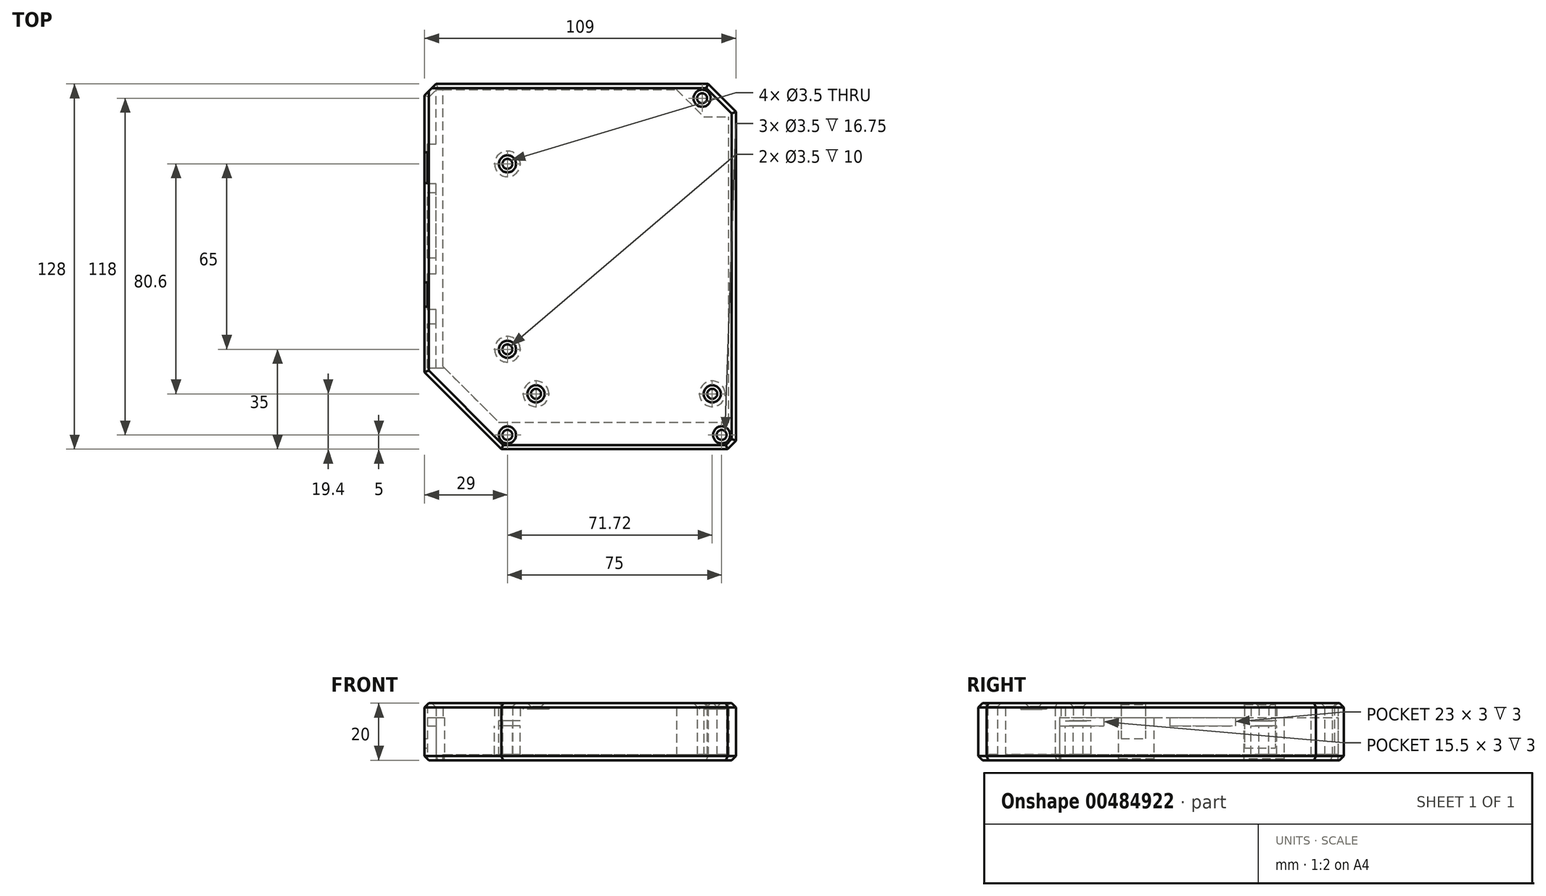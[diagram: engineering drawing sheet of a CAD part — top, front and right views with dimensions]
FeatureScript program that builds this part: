
annotation { "Feature Type Name" : "Feature", "Feature Type Description" : "" }
export const myFeature = defineFeature(function(context is Context, id is Id, definition is map)
    precondition{}
    {
        {
            var Q0;
            Q0=qCreatedBy(makeId("Top.planeOp"),FACE);
            var sketch = newSketch(context, id + "F0", { "sketchPlane" : qUnion([Q0])});
            skLineSegment(sketch, "E0.bottom", {"start": v(-53.5, 61) * mm, "end": v(30.5, 61) * mm, "construction": true});
            skLineSegment(sketch, "E0.top", {"start": v(-53.5, -35) * mm, "end": v(30.5, -35) * mm, "construction": true});
            skLineSegment(sketch, "E0.left", {"start": v(-53.5, 61) * mm, "end": v(-53.5, -35) * mm, "construction": true});
            skLineSegment(sketch, "E0.right", {"start": v(30.5, 61) * mm, "end": v(30.5, -35) * mm, "construction": true});
            skLineSegment(sketch, "E1.bottom", {"start": v(-19.5, 52) * mm, "end": v(51.5, 52) * mm, "construction": true});
            skLineSegment(sketch, "E1.top", {"start": v(-19.5, -54) * mm, "end": v(51.5, -54) * mm, "construction": true});
            skLineSegment(sketch, "E1.left", {"start": v(-19.5, 52) * mm, "end": v(-19.5, -54) * mm, "construction": true});
            skLineSegment(sketch, "E1.right", {"start": v(51.5, 52) * mm, "end": v(51.5, -54) * mm, "construction": true});
            skLineSegment(sketch, "E2.bottom", {"start": v(54.5, 64) * mm, "end": v(-54.5, 64) * mm, "construction": true});
            skLineSegment(sketch, "E2.top", {"start": v(54.5, -64) * mm, "end": v(-54.5, -64) * mm, "construction": true});
            skLineSegment(sketch, "E2.left", {"start": v(54.5, 64) * mm, "end": v(54.5, -64) * mm, "construction": true});
            skLineSegment(sketch, "E2.right", {"start": v(-54.5, 64) * mm, "end": v(-54.5, -64) * mm, "construction": true});
            skPoint(sketch, "E2.middle", {"position": v(0, 0) * mm});
            skPoint(sketch, "E3", {"position": v(-25.5, -29) * mm});
            skPoint(sketch, "E4", {"position": v(-25.5, 36) * mm});
            skPoint(sketch, "E5", {"position": v(-25.5, -59) * mm});
            skPoint(sketch, "E6", {"position": v(49.5, -59) * mm});
            skSolve(sketch);
        }
        {
            var Q0;
            Q0=qCreatedBy(makeId("Top.planeOp"),FACE);
            var sketch = newSketch(context, id + "F1", { "sketchPlane" : qUnion([Q0])});
            skLineSegment(sketch, "E7", {"start": v(-54.5, -37.07) * mm, "end": v(-27.57, -64) * mm});
            skLineSegment(sketch, "E8", {"start": v(-27.57, -64) * mm, "end": v(51.57, -64) * mm});
            skLineSegment(sketch, "E9", {"start": v(51.57, -64) * mm, "end": v(54.5, -61.07) * mm});
            skLineSegment(sketch, "E10", {"start": v(54.5, -61.07) * mm, "end": v(54.5, 54.24) * mm});
            skLineSegment(sketch, "E11", {"start": v(54.5, 54.24) * mm, "end": v(44.74, 64) * mm});
            skLineSegment(sketch, "E12", {"start": v(44.74, 64) * mm, "end": v(-50.5, 64) * mm});
            skLineSegment(sketch, "E13", {"start": v(-54.5, 60) * mm, "end": v(-54.5, -37.07) * mm});
            skCircle(sketch, "E14", {"center": v(42.67, 59) * mm, "radius": 1.75 * mm});
            skCircle(sketch, "E15", {"center": v(-25.5, 36) * mm, "radius": 1.75 * mm});
            skCircle(sketch, "E16", {"center": v(-25.5, -29) * mm, "radius": 1.75 * mm});
            skCircle(sketch, "E17", {"center": v(-25.5, -59) * mm, "radius": 1.75 * mm});
            skCircle(sketch, "E18", {"center": v(49.5, -59) * mm, "radius": 1.75 * mm});
            skLineSegment(sketch, "E19", {"start": v(-48.09, -35) * mm, "end": v(-53.5, -35) * mm, "construction": true});
            skLineSegment(sketch, "E20", {"start": v(-53.5, -35) * mm, "end": v(-53.5, -20) * mm});
            skLineSegment(sketch, "E21", {"start": v(-53.5, -20) * mm, "end": v(-50.5, -20) * mm});
            skLineSegment(sketch, "E22", {"start": v(-50.5, -20) * mm, "end": v(-50.5, -15) * mm});
            skLineSegment(sketch, "E23", {"start": v(-50.5, -15) * mm, "end": v(-53.5, -15) * mm});
            skLineSegment(sketch, "E24", {"start": v(-48.09, -35) * mm, "end": v(-28.59, -54.5) * mm});
            skLineSegment(sketch, "E25", {"start": v(-28.59, -54.5) * mm, "end": v(52, -54.5) * mm});
            skLineSegment(sketch, "E26", {"start": v(52, -54.5) * mm, "end": v(52, 52.5) * mm});
            skLineSegment(sketch, "E27", {"start": v(-53.5, -15) * mm, "end": v(-53.5, -2.5) * mm});
            skLineSegment(sketch, "E28", {"start": v(-53.5, -2.5) * mm, "end": v(-50.5, -2.5) * mm});
            skLineSegment(sketch, "E29", {"start": v(-50.5, -2.5) * mm, "end": v(-50.5, 3) * mm});
            skLineSegment(sketch, "E30", {"start": v(-50.5, 3) * mm, "end": v(-53.5, 3) * mm});
            skLineSegment(sketch, "E31", {"start": v(-53.5, 3) * mm, "end": v(-53.5, 26) * mm});
            skLineSegment(sketch, "E32", {"start": v(-53.5, 26) * mm, "end": v(-50.5, 26) * mm});
            skLineSegment(sketch, "E33", {"start": v(-50.5, 26) * mm, "end": v(-50.5, 29) * mm});
            skLineSegment(sketch, "E34", {"start": v(-50.5, 29) * mm, "end": v(-53.5, 29) * mm});
            skLineSegment(sketch, "E35", {"start": v(-53.5, 29) * mm, "end": v(-53.5, 43) * mm});
            skLineSegment(sketch, "E36", {"start": v(-53.5, 43) * mm, "end": v(-50.5, 43) * mm});
            skLineSegment(sketch, "E37", {"start": v(-50.5, 62) * mm, "end": v(33.74, 62) * mm});
            skLineSegment(sketch, "E38", {"start": v(33.74, 62) * mm, "end": v(43.24, 52.5) * mm});
            skLineSegment(sketch, "E39", {"start": v(43.24, 52.5) * mm, "end": v(52, 52.5) * mm});
            skLineSegment(sketch, "E40", {"start": v(-50.5, 43) * mm, "end": v(-50.5, 50) * mm});
            skLineSegment(sketch, "E41", {"start": v(-53.5, -35) * mm, "end": v(-53.5, -35.5) * mm});
            skLineSegment(sketch, "E42", {"start": v(-53.5, -35.5) * mm, "end": v(-47.59, -35.5) * mm});
            skLineSegment(sketch, "E43", {"start": v(-48.09, -35) * mm, "end": v(-48.09, 62) * mm});
            skCircle(sketch, "E44", {"center": v(-15.5, -44.6) * mm, "radius": 1.75 * mm});
            skCircle(sketch, "E45", {"center": v(46.22, -44.6) * mm, "radius": 1.75 * mm});
            skCircle(sketch, "E46", {"center": v(-25.5, 36) * mm, "radius": 4.5 * mm});
            skCircle(sketch, "E47", {"center": v(-25.5, -29) * mm, "radius": 4.5 * mm});
            skCircle(sketch, "E48", {"center": v(46.22, -44.6) * mm, "radius": 4.5 * mm});
            skCircle(sketch, "E49", {"center": v(-15.5, -44.6) * mm, "radius": 4.5 * mm});
            skLineSegment(sketch, "E50", {"start": v(-50.5, 64) * mm, "end": v(-54.5, 60) * mm});
            skLineSegment(sketch, "E51", {"start": v(-50.5, 50) * mm, "end": v(-50.5, 62) * mm});
            skSolve(sketch);
        }
        {
            var Q0;
            Q0=makeQuery(id+"F1.imprint","IMPRINT",FACE,{"disambiguationData":[TD([[makeQuery(id+"F1.imprint","IMPRINT",EDGE,{"derivedFrom":sQuery(id+"F1.wireOp",EDGE,"E7")}),1.0]])]});
            extrude(context, id + "F2", {"entities" : qUnion([Q0]), "depth" : 8 * mm});
        }
        {
            var Q0;
            {var subQ5=sQuery(id+"F1.wireOp",EDGE,"E25");Q0=makeQuery(id+"F1.imprint","IMPRINT",FACE,{"disambiguationData":[TD([[makeQuery(id+"F1.imprint","IMPRINT",EDGE,{"derivedFrom":subQ5}),1.0]])]});}
            var Q1;
            Q1=makeQuery(id+"F2.opExtrude","CAP_FACE",FACE,{"disambiguationData":[OSD([sQuery(id+"F1.wireOp",EDGE,"E7"),sQuery(id+"F1.wireOp",EDGE,"E8"),sQuery(id+"F1.wireOp",EDGE,"E9"),sQuery(id+"F1.wireOp",EDGE,"E10"),sQuery(id+"F1.wireOp",EDGE,"E11"),sQuery(id+"F1.wireOp",EDGE,"E12"),sQuery(id+"F1.wireOp",EDGE,"gnJz5Qc8-ZNcq-LTVa-uIN5-WBNiVvJ7uBc6"),sQuery(id+"F1.wireOp",EDGE,"E13"),sQuery(id+"F1.wireOp",EDGE,"E14"),sQuery(id+"F1.wireOp",EDGE,"E17"),sQuery(id+"F1.wireOp",EDGE,"E18"),sQuery(id+"F1.wireOp",EDGE,"E20"),sQuery(id+"F1.wireOp",EDGE,"E21"),sQuery(id+"F1.wireOp",EDGE,"E22"),sQuery(id+"F1.wireOp",EDGE,"E23"),sQuery(id+"F1.wireOp",EDGE,"E24"),sQuery(id+"F1.wireOp",EDGE,"E25"),sQuery(id+"F1.wireOp",EDGE,"E26"),sQuery(id+"F1.wireOp",EDGE,"E27"),sQuery(id+"F1.wireOp",EDGE,"E28"),sQuery(id+"F1.wireOp",EDGE,"E29"),sQuery(id+"F1.wireOp",EDGE,"E30"),sQuery(id+"F1.wireOp",EDGE,"E31"),sQuery(id+"F1.wireOp",EDGE,"E32"),sQuery(id+"F1.wireOp",EDGE,"E33"),sQuery(id+"F1.wireOp",EDGE,"E34"),sQuery(id+"F1.wireOp",EDGE,"E35"),sQuery(id+"F1.wireOp",EDGE,"E36"),sQuery(id+"F1.wireOp",EDGE,"E37"),sQuery(id+"F1.wireOp",EDGE,"E38"),sQuery(id+"F1.wireOp",EDGE,"E39"),sQuery(id+"F1.wireOp",EDGE,"E40"),sQuery(id+"F1.wireOp",EDGE,"4yesmApJ-FmPo-i4KC-uSoO-ILCi17epRu4C"),sQuery(id+"F1.wireOp",EDGE,"E41"),sQuery(id+"F1.wireOp",EDGE,"E42")])],"isStart":false});
            extrude(context, id + "F3", {"entities" : qUnion([Q0]), "operationType" : NewBodyOperationType.ADD, "endBound" : BoundingType.UP_TO_SURFACE, "endBoundEntityFace" : qUnion([Q1]), "depth" : 25 * mm, "hasSecondDirection" : true, "secondDirectionOppositeDirection" : false, "secondDirectionDepth" : 6.4 * mm});
        }
        {
            var Q0;
            Q0=makeQuery(id+"F1.imprint","IMPRINT",FACE,{"disambiguationData":[TD([[makeQuery(id+"F1.imprint","IMPRINT",EDGE,{"derivedFrom":sQuery(id+"F1.wireOp",EDGE,"E20")}),-1.0]])]});
            var Q1;
            {var subQ0=sQuery(id+"F1.wireOp",EDGE,"E39");var subQ1=sQuery(id+"F1.wireOp",EDGE,"E38");var subQ2=sQuery(id+"F1.wireOp",EDGE,"E37");var subQ3=sQuery(id+"F1.wireOp",EDGE,"E26");var subQ4=sQuery(id+"F1.wireOp",EDGE,"E25");var subQ5=sQuery(id+"F1.wireOp",EDGE,"E24");Q1=makeQuery(id+"F3.boolean.opBoolean","MERGE",FACE,{"derivedFrom":[makeQuery(id+"F2.opExtrude","CAP_FACE",FACE,{"disambiguationData":[OSD([sQuery(id+"F1.wireOp",EDGE,"E7"),sQuery(id+"F1.wireOp",EDGE,"E8"),sQuery(id+"F1.wireOp",EDGE,"E9"),sQuery(id+"F1.wireOp",EDGE,"E10"),sQuery(id+"F1.wireOp",EDGE,"E11"),sQuery(id+"F1.wireOp",EDGE,"E12"),sQuery(id+"F1.wireOp",EDGE,"E13"),sQuery(id+"F1.wireOp",EDGE,"E14"),sQuery(id+"F1.wireOp",EDGE,"E17"),sQuery(id+"F1.wireOp",EDGE,"E18"),sQuery(id+"F1.wireOp",EDGE,"E20"),sQuery(id+"F1.wireOp",EDGE,"E21"),sQuery(id+"F1.wireOp",EDGE,"E22"),sQuery(id+"F1.wireOp",EDGE,"E23"),subQ5,subQ4,subQ3,sQuery(id+"F1.wireOp",EDGE,"E27"),sQuery(id+"F1.wireOp",EDGE,"E28"),sQuery(id+"F1.wireOp",EDGE,"E29"),sQuery(id+"F1.wireOp",EDGE,"E30"),sQuery(id+"F1.wireOp",EDGE,"E31"),sQuery(id+"F1.wireOp",EDGE,"E32"),sQuery(id+"F1.wireOp",EDGE,"E33"),sQuery(id+"F1.wireOp",EDGE,"E34"),sQuery(id+"F1.wireOp",EDGE,"E35"),sQuery(id+"F1.wireOp",EDGE,"E36"),subQ2,subQ1,subQ0,sQuery(id+"F1.wireOp",EDGE,"E40"),sQuery(id+"F1.wireOp",EDGE,"E41"),sQuery(id+"F1.wireOp",EDGE,"E42"),sQuery(id+"F1.wireOp",EDGE,"E50"),sQuery(id+"F1.wireOp",EDGE,"E51")])],"isStart":false}),makeQuery(id+"F3.opExtrude","CAP_FACE",FACE,{"disambiguationData":[OSD([subQ5,subQ4,subQ3,subQ2,subQ1,subQ0,sQuery(id+"F1.wireOp",EDGE,"E43"),sQuery(id+"F1.wireOp",EDGE,"E46"),sQuery(id+"F1.wireOp",EDGE,"E47"),sQuery(id+"F1.wireOp",EDGE,"E48"),sQuery(id+"F1.wireOp",EDGE,"E49")])],"isStart":false})]});}
            extrude(context, id + "F4", {"entities" : qUnion([Q0]), "operationType" : NewBodyOperationType.ADD, "endBound" : BoundingType.UP_TO_SURFACE, "endBoundEntityFace" : qUnion([Q1]), "depth" : 25 * mm, "hasSecondDirection" : true, "secondDirectionOppositeDirection" : false, "secondDirectionDepth" : 3 * mm});
        }
        {
            var Q0;
            Q0=makeQuery(id+"F1.imprint","IMPRINT",FACE,{"disambiguationData":[TD([[makeQuery(id+"F1.imprint","IMPRINT",EDGE,{"derivedFrom":sQuery(id+"F1.wireOp",EDGE,"E16")}),-1.0]])]});
            var Q1;
            Q1=makeQuery(id+"F1.imprint","IMPRINT",FACE,{"disambiguationData":[TD([[makeQuery(id+"F1.imprint","IMPRINT",EDGE,{"derivedFrom":sQuery(id+"F1.wireOp",EDGE,"E15")}),-1.0]])]});
            var Q2;
            {var subQ0=sQuery(id+"F1.wireOp",EDGE,"E51");var subQ1=sQuery(id+"F1.wireOp",EDGE,"E43");var subQ2=sQuery(id+"F1.wireOp",EDGE,"E42");var subQ3=sQuery(id+"F1.wireOp",EDGE,"E41");var subQ4=sQuery(id+"F1.wireOp",EDGE,"E40");var subQ5=sQuery(id+"F1.wireOp",EDGE,"E37");var subQ6=sQuery(id+"F1.wireOp",EDGE,"E36");var subQ7=sQuery(id+"F1.wireOp",EDGE,"E35");var subQ8=sQuery(id+"F1.wireOp",EDGE,"E34");var subQ9=sQuery(id+"F1.wireOp",EDGE,"E33");var subQ10=sQuery(id+"F1.wireOp",EDGE,"E32");var subQ11=sQuery(id+"F1.wireOp",EDGE,"E31");var subQ12=sQuery(id+"F1.wireOp",EDGE,"E30");var subQ13=sQuery(id+"F1.wireOp",EDGE,"E29");var subQ14=sQuery(id+"F1.wireOp",EDGE,"E28");var subQ15=sQuery(id+"F1.wireOp",EDGE,"E27");var subQ16=sQuery(id+"F1.wireOp",EDGE,"E24");var subQ17=sQuery(id+"F1.wireOp",EDGE,"E23");var subQ18=sQuery(id+"F1.wireOp",EDGE,"E22");var subQ19=sQuery(id+"F1.wireOp",EDGE,"E21");var subQ20=sQuery(id+"F1.wireOp",EDGE,"E20");var subQ21=sQuery(id+"F1.wireOp",EDGE,"E39");var subQ22=sQuery(id+"F1.wireOp",EDGE,"E38");var subQ23=sQuery(id+"F1.wireOp",EDGE,"E26");var subQ24=sQuery(id+"F1.wireOp",EDGE,"E25");Q2=makeQuery(id+"F4.boolean.opBoolean","MERGE",FACE,{"derivedFrom":[makeQuery(id+"F3.boolean.opBoolean","MERGE",FACE,{"derivedFrom":[makeQuery(id+"F2.opExtrude","CAP_FACE",FACE,{"disambiguationData":[OSD([sQuery(id+"F1.wireOp",EDGE,"E7"),sQuery(id+"F1.wireOp",EDGE,"E8"),sQuery(id+"F1.wireOp",EDGE,"E9"),sQuery(id+"F1.wireOp",EDGE,"E10"),sQuery(id+"F1.wireOp",EDGE,"E11"),sQuery(id+"F1.wireOp",EDGE,"E12"),sQuery(id+"F1.wireOp",EDGE,"E13"),sQuery(id+"F1.wireOp",EDGE,"E14"),sQuery(id+"F1.wireOp",EDGE,"E17"),sQuery(id+"F1.wireOp",EDGE,"E18"),subQ20,subQ19,subQ18,subQ17,subQ16,subQ24,subQ23,subQ15,subQ14,subQ13,subQ12,subQ11,subQ10,subQ9,subQ8,subQ7,subQ6,subQ5,subQ22,subQ21,subQ4,subQ3,subQ2,sQuery(id+"F1.wireOp",EDGE,"E50"),subQ0])],"isStart":false}),makeQuery(id+"F3.opExtrude","CAP_FACE",FACE,{"disambiguationData":[OSD([subQ16,subQ24,subQ23,subQ5,subQ22,subQ21,subQ1,sQuery(id+"F1.wireOp",EDGE,"E46"),sQuery(id+"F1.wireOp",EDGE,"E47"),sQuery(id+"F1.wireOp",EDGE,"E48"),sQuery(id+"F1.wireOp",EDGE,"E49")])],"isStart":false})]}),makeQuery(id+"F4.opExtrude","CAP_FACE",FACE,{"disambiguationData":[OSD([subQ20,subQ19,subQ18,subQ17,subQ16,subQ15,subQ14,subQ13,subQ12,subQ11,subQ10,subQ9,subQ8,subQ7,subQ6,subQ5,subQ4,subQ3,subQ2,subQ1,subQ0])],"isStart":false})]});}
            extrude(context, id + "F5", {"entities" : qUnion([Q0, Q1]), "operationType" : NewBodyOperationType.ADD, "endBound" : BoundingType.UP_TO_SURFACE, "endBoundEntityFace" : qUnion([Q2]), "depth" : 25 * mm, "hasSecondDirection" : true, "secondDirectionOppositeDirection" : false, "secondDirectionDepth" : 1.8 * mm});
        }
        {
            var Q0;
            Q0=makeQuery(id+"F1.imprint","IMPRINT",FACE,{"disambiguationData":[TD([[makeQuery(id+"F1.imprint","IMPRINT",EDGE,{"derivedFrom":sQuery(id+"F1.wireOp",EDGE,"E44")}),-1.0]])]});
            var Q1;
            Q1=makeQuery(id+"F1.imprint","IMPRINT",FACE,{"disambiguationData":[TD([[makeQuery(id+"F1.imprint","IMPRINT",EDGE,{"derivedFrom":sQuery(id+"F1.wireOp",EDGE,"E45")}),-1.0]])]});
            var Q2;
            {var subQ0=sQuery(id+"F1.wireOp",EDGE,"E47");var subQ1=sQuery(id+"F1.wireOp",EDGE,"E46");var subQ2=sQuery(id+"F1.wireOp",EDGE,"E51");var subQ3=sQuery(id+"F1.wireOp",EDGE,"E43");var subQ4=sQuery(id+"F1.wireOp",EDGE,"E42");var subQ5=sQuery(id+"F1.wireOp",EDGE,"E41");var subQ6=sQuery(id+"F1.wireOp",EDGE,"E40");var subQ7=sQuery(id+"F1.wireOp",EDGE,"E37");var subQ8=sQuery(id+"F1.wireOp",EDGE,"E36");var subQ9=sQuery(id+"F1.wireOp",EDGE,"E35");var subQ10=sQuery(id+"F1.wireOp",EDGE,"E34");var subQ11=sQuery(id+"F1.wireOp",EDGE,"E33");var subQ12=sQuery(id+"F1.wireOp",EDGE,"E32");var subQ13=sQuery(id+"F1.wireOp",EDGE,"E31");var subQ14=sQuery(id+"F1.wireOp",EDGE,"E30");var subQ15=sQuery(id+"F1.wireOp",EDGE,"E29");var subQ16=sQuery(id+"F1.wireOp",EDGE,"E28");var subQ17=sQuery(id+"F1.wireOp",EDGE,"E27");var subQ18=sQuery(id+"F1.wireOp",EDGE,"E24");var subQ19=sQuery(id+"F1.wireOp",EDGE,"E23");var subQ20=sQuery(id+"F1.wireOp",EDGE,"E22");var subQ21=sQuery(id+"F1.wireOp",EDGE,"E21");var subQ22=sQuery(id+"F1.wireOp",EDGE,"E20");var subQ23=sQuery(id+"F1.wireOp",EDGE,"E39");var subQ24=sQuery(id+"F1.wireOp",EDGE,"E38");var subQ25=sQuery(id+"F1.wireOp",EDGE,"E26");var subQ26=sQuery(id+"F1.wireOp",EDGE,"E25");Q2=makeQuery(id+"F5.boolean.opBoolean","MERGE",FACE,{"derivedFrom":[makeQuery(id+"F4.boolean.opBoolean","MERGE",FACE,{"derivedFrom":[makeQuery(id+"F3.boolean.opBoolean","MERGE",FACE,{"derivedFrom":[makeQuery(id+"F2.opExtrude","CAP_FACE",FACE,{"disambiguationData":[OSD([sQuery(id+"F1.wireOp",EDGE,"E7"),sQuery(id+"F1.wireOp",EDGE,"E8"),sQuery(id+"F1.wireOp",EDGE,"E9"),sQuery(id+"F1.wireOp",EDGE,"E10"),sQuery(id+"F1.wireOp",EDGE,"E11"),sQuery(id+"F1.wireOp",EDGE,"E12"),sQuery(id+"F1.wireOp",EDGE,"E13"),sQuery(id+"F1.wireOp",EDGE,"E14"),sQuery(id+"F1.wireOp",EDGE,"E17"),sQuery(id+"F1.wireOp",EDGE,"E18"),subQ22,subQ21,subQ20,subQ19,subQ18,subQ26,subQ25,subQ17,subQ16,subQ15,subQ14,subQ13,subQ12,subQ11,subQ10,subQ9,subQ8,subQ7,subQ24,subQ23,subQ6,subQ5,subQ4,sQuery(id+"F1.wireOp",EDGE,"E50"),subQ2])],"isStart":false}),makeQuery(id+"F3.opExtrude","CAP_FACE",FACE,{"disambiguationData":[OSD([subQ18,subQ26,subQ25,subQ7,subQ24,subQ23,subQ3,subQ1,subQ0,sQuery(id+"F1.wireOp",EDGE,"E48"),sQuery(id+"F1.wireOp",EDGE,"E49")])],"isStart":false})]}),makeQuery(id+"F4.opExtrude","CAP_FACE",FACE,{"disambiguationData":[OSD([subQ22,subQ21,subQ20,subQ19,subQ18,subQ17,subQ16,subQ15,subQ14,subQ13,subQ12,subQ11,subQ10,subQ9,subQ8,subQ7,subQ6,subQ5,subQ4,subQ3,subQ2])],"isStart":false})]}),makeQuery(id+"F5.opExtrude","CAP_FACE",FACE,{"disambiguationData":[OSD([sQuery(id+"F1.wireOp",EDGE,"E15"),subQ1])],"isStart":false}),makeQuery(id+"F5.opExtrude","CAP_FACE",FACE,{"disambiguationData":[OSD([sQuery(id+"F1.wireOp",EDGE,"E16"),subQ0])],"isStart":false})]});}
            extrude(context, id + "F6", {"entities" : qUnion([Q0, Q1]), "operationType" : NewBodyOperationType.ADD, "endBound" : BoundingType.UP_TO_SURFACE, "endBoundEntityFace" : qUnion([Q2]), "depth" : 25 * mm, "hasSecondDirection" : true, "secondDirectionOppositeDirection" : false, "secondDirectionDepth" : 5.8 * mm});
        }
        {
            var Q0;
            {var subQ0=sQuery(id+"F1.wireOp",EDGE,"E48");var subQ1=sQuery(id+"F1.wireOp",EDGE,"E49");var subQ2=sQuery(id+"F1.wireOp",EDGE,"E47");var subQ3=sQuery(id+"F1.wireOp",EDGE,"E46");var subQ4=sQuery(id+"F1.wireOp",EDGE,"E51");var subQ5=sQuery(id+"F1.wireOp",EDGE,"E43");var subQ6=sQuery(id+"F1.wireOp",EDGE,"E42");var subQ7=sQuery(id+"F1.wireOp",EDGE,"E41");var subQ8=sQuery(id+"F1.wireOp",EDGE,"E40");var subQ9=sQuery(id+"F1.wireOp",EDGE,"E37");var subQ10=sQuery(id+"F1.wireOp",EDGE,"E36");var subQ11=sQuery(id+"F1.wireOp",EDGE,"E35");var subQ12=sQuery(id+"F1.wireOp",EDGE,"E34");var subQ13=sQuery(id+"F1.wireOp",EDGE,"E33");var subQ14=sQuery(id+"F1.wireOp",EDGE,"E32");var subQ15=sQuery(id+"F1.wireOp",EDGE,"E31");var subQ16=sQuery(id+"F1.wireOp",EDGE,"E30");var subQ17=sQuery(id+"F1.wireOp",EDGE,"E29");var subQ18=sQuery(id+"F1.wireOp",EDGE,"E28");var subQ19=sQuery(id+"F1.wireOp",EDGE,"E27");var subQ20=sQuery(id+"F1.wireOp",EDGE,"E24");var subQ21=sQuery(id+"F1.wireOp",EDGE,"E23");var subQ22=sQuery(id+"F1.wireOp",EDGE,"E22");var subQ23=sQuery(id+"F1.wireOp",EDGE,"E21");var subQ24=sQuery(id+"F1.wireOp",EDGE,"E20");var subQ25=sQuery(id+"F1.wireOp",EDGE,"E39");var subQ26=sQuery(id+"F1.wireOp",EDGE,"E38");var subQ27=sQuery(id+"F1.wireOp",EDGE,"E26");var subQ28=sQuery(id+"F1.wireOp",EDGE,"E25");Q0=makeQuery(id+"F6.boolean.opBoolean","MERGE",FACE,{"derivedFrom":[makeQuery(id+"F5.boolean.opBoolean","MERGE",FACE,{"derivedFrom":[makeQuery(id+"F4.boolean.opBoolean","MERGE",FACE,{"derivedFrom":[makeQuery(id+"F3.boolean.opBoolean","MERGE",FACE,{"derivedFrom":[makeQuery(id+"F2.opExtrude","CAP_FACE",FACE,{"disambiguationData":[OSD([sQuery(id+"F1.wireOp",EDGE,"E7"),sQuery(id+"F1.wireOp",EDGE,"E8"),sQuery(id+"F1.wireOp",EDGE,"E9"),sQuery(id+"F1.wireOp",EDGE,"E10"),sQuery(id+"F1.wireOp",EDGE,"E11"),sQuery(id+"F1.wireOp",EDGE,"E12"),sQuery(id+"F1.wireOp",EDGE,"E13"),sQuery(id+"F1.wireOp",EDGE,"E14"),sQuery(id+"F1.wireOp",EDGE,"E17"),sQuery(id+"F1.wireOp",EDGE,"E18"),subQ24,subQ23,subQ22,subQ21,subQ20,subQ28,subQ27,subQ19,subQ18,subQ17,subQ16,subQ15,subQ14,subQ13,subQ12,subQ11,subQ10,subQ9,subQ26,subQ25,subQ8,subQ7,subQ6,sQuery(id+"F1.wireOp",EDGE,"E50"),subQ4])],"isStart":false}),makeQuery(id+"F3.opExtrude","CAP_FACE",FACE,{"disambiguationData":[OSD([subQ20,subQ28,subQ27,subQ9,subQ26,subQ25,subQ5,subQ3,subQ2,subQ0,subQ1])],"isStart":false})]}),makeQuery(id+"F4.opExtrude","CAP_FACE",FACE,{"disambiguationData":[OSD([subQ24,subQ23,subQ22,subQ21,subQ20,subQ19,subQ18,subQ17,subQ16,subQ15,subQ14,subQ13,subQ12,subQ11,subQ10,subQ9,subQ8,subQ7,subQ6,subQ5,subQ4])],"isStart":false})]}),makeQuery(id+"F5.opExtrude","CAP_FACE",FACE,{"disambiguationData":[OSD([sQuery(id+"F1.wireOp",EDGE,"E15"),subQ3])],"isStart":false}),makeQuery(id+"F5.opExtrude","CAP_FACE",FACE,{"disambiguationData":[OSD([sQuery(id+"F1.wireOp",EDGE,"E16"),subQ2])],"isStart":false})]}),makeQuery(id+"F6.opExtrude","CAP_FACE",FACE,{"disambiguationData":[OSD([sQuery(id+"F1.wireOp",EDGE,"E44"),subQ1])],"isStart":false}),makeQuery(id+"F6.opExtrude","CAP_FACE",FACE,{"disambiguationData":[OSD([sQuery(id+"F1.wireOp",EDGE,"E45"),subQ0])],"isStart":false})]});}
            var sketch = newSketch(context, id + "F7", { "sketchPlane" : qUnion([Q0])});
            skCircle(sketch, "E52", {"center": v(-25.5, 36) * mm, "radius": 3 * mm});
            skCircle(sketch, "E53", {"center": v(42.67, 59) * mm, "radius": 3 * mm});
            skCircle(sketch, "E54", {"center": v(-25.5, -29) * mm, "radius": 3 * mm});
            skCircle(sketch, "E55", {"center": v(-25.5, -59) * mm, "radius": 3 * mm});
            skCircle(sketch, "E56", {"center": v(-15.5, -44.6) * mm, "radius": 3 * mm});
            skCircle(sketch, "E57", {"center": v(46.22, -44.6) * mm, "radius": 3 * mm});
            skCircle(sketch, "E58", {"center": v(49.5, -59) * mm, "radius": 3 * mm});
            skSolve(sketch);
        }
        {
            var Q0;
            Q0=makeQuery(id+"F7.imprint","IMPRINT",FACE,{"disambiguationData":[TD([[makeQuery(id+"F7.imprint","IMPRINT",EDGE,{"derivedFrom":sQuery(id+"F7.wireOp",EDGE,"E55")}),1.0]])]});
            var Q1;
            Q1=makeQuery(id+"F7.imprint","IMPRINT",FACE,{"disambiguationData":[TD([[makeQuery(id+"F7.imprint","IMPRINT",EDGE,{"derivedFrom":makeQuery(id+"F2.opExtrude","CAP_EDGE",EDGE,{"disambiguationData":[OSD([sQuery(id+"F1.wireOp",EDGE,"E17")])],"isStart":false})}),1.0]])]});
            var Q2;
            Q2=makeQuery(id+"F7.imprint","IMPRINT",FACE,{"disambiguationData":[TD([[makeQuery(id+"F7.imprint","IMPRINT",EDGE,{"derivedFrom":sQuery(id+"F7.wireOp",EDGE,"E56")}),1.0]])]});
            var Q3;
            Q3=makeQuery(id+"F7.imprint","IMPRINT",FACE,{"disambiguationData":[TD([[makeQuery(id+"F7.imprint","IMPRINT",EDGE,{"derivedFrom":makeQuery(id+"F6.opExtrude","CAP_EDGE",EDGE,{"disambiguationData":[OSD([sQuery(id+"F1.wireOp",EDGE,"E44")])],"isStart":false})}),1.0]])]});
            var Q4;
            Q4=makeQuery(id+"F7.imprint","IMPRINT",FACE,{"disambiguationData":[TD([[makeQuery(id+"F7.imprint","IMPRINT",EDGE,{"derivedFrom":makeQuery(id+"F5.opExtrude","CAP_EDGE",EDGE,{"disambiguationData":[OSD([sQuery(id+"F1.wireOp",EDGE,"E16")])],"isStart":false})}),1.0]])]});
            var Q5;
            Q5=makeQuery(id+"F7.imprint","IMPRINT",FACE,{"disambiguationData":[TD([[makeQuery(id+"F7.imprint","IMPRINT",EDGE,{"derivedFrom":sQuery(id+"F7.wireOp",EDGE,"E54")}),1.0]])]});
            var Q6;
            Q6=makeQuery(id+"F7.imprint","IMPRINT",FACE,{"disambiguationData":[TD([[makeQuery(id+"F7.imprint","IMPRINT",EDGE,{"derivedFrom":makeQuery(id+"F6.opExtrude","CAP_EDGE",EDGE,{"disambiguationData":[OSD([sQuery(id+"F1.wireOp",EDGE,"E45")])],"isStart":false})}),1.0]])]});
            var Q7;
            Q7=makeQuery(id+"F7.imprint","IMPRINT",FACE,{"disambiguationData":[TD([[makeQuery(id+"F7.imprint","IMPRINT",EDGE,{"derivedFrom":sQuery(id+"F7.wireOp",EDGE,"E57")}),1.0]])]});
            var Q8;
            Q8=makeQuery(id+"F7.imprint","IMPRINT",FACE,{"disambiguationData":[TD([[makeQuery(id+"F7.imprint","IMPRINT",EDGE,{"derivedFrom":makeQuery(id+"F2.opExtrude","CAP_EDGE",EDGE,{"disambiguationData":[OSD([sQuery(id+"F1.wireOp",EDGE,"E14")])],"isStart":false})}),1.0]])]});
            var Q9;
            Q9=makeQuery(id+"F7.imprint","IMPRINT",FACE,{"disambiguationData":[TD([[makeQuery(id+"F7.imprint","IMPRINT",EDGE,{"derivedFrom":sQuery(id+"F7.wireOp",EDGE,"E53")}),1.0]])]});
            var Q10;
            Q10=makeQuery(id+"F7.imprint","IMPRINT",FACE,{"disambiguationData":[TD([[makeQuery(id+"F7.imprint","IMPRINT",EDGE,{"derivedFrom":makeQuery(id+"F5.opExtrude","CAP_EDGE",EDGE,{"disambiguationData":[OSD([sQuery(id+"F1.wireOp",EDGE,"E15")])],"isStart":false})}),1.0]])]});
            var Q11;
            Q11=makeQuery(id+"F7.imprint","IMPRINT",FACE,{"disambiguationData":[TD([[makeQuery(id+"F7.imprint","IMPRINT",EDGE,{"derivedFrom":sQuery(id+"F7.wireOp",EDGE,"E52")}),1.0]])]});
            var Q12;
            Q12=makeQuery(id+"F7.imprint","IMPRINT",FACE,{"disambiguationData":[TD([[makeQuery(id+"F7.imprint","IMPRINT",EDGE,{"derivedFrom":makeQuery(id+"F2.opExtrude","CAP_EDGE",EDGE,{"disambiguationData":[OSD([sQuery(id+"F1.wireOp",EDGE,"E18")])],"isStart":false})}),1.0]])]});
            var Q13;
            Q13=makeQuery(id+"F7.imprint","IMPRINT",FACE,{"disambiguationData":[TD([[makeQuery(id+"F7.imprint","IMPRINT",EDGE,{"derivedFrom":sQuery(id+"F7.wireOp",EDGE,"E58")}),1.0]])]});
            extrude(context, id + "F8", {"entities" : qUnion([Q0, Q1, Q2, Q3, Q4, Q5, Q6, Q7, Q8, Q9, Q10, Q11, Q12, Q13]), "operationType" : NewBodyOperationType.REMOVE, "endBound" : BoundingType.THROUGH_ALL, "oppositeDirection" : true, "depth" : 25 * mm, "hasDraft" : true, "draftAngle" : 45 * degree, "draftPullDirection" : true});
        }
        {
            var Q0;
            Q0=makeQuery(id+"F1.imprint","IMPRINT",FACE,{"disambiguationData":[TD([[makeQuery(id+"F1.imprint","IMPRINT",EDGE,{"derivedFrom":sQuery(id+"F1.wireOp",EDGE,"E7")}),1.0]])]});
            extrude(context, id + "F9", {"entities" : qUnion([Q0]), "oppositeDirection" : true, "depth" : 12 * mm, "offsetDistance" : 25 * mm});
        }
        {
            var Q0;
            {var subQ5=sQuery(id+"F1.wireOp",EDGE,"E25");Q0=makeQuery(id+"F1.imprint","IMPRINT",FACE,{"disambiguationData":[TD([[makeQuery(id+"F1.imprint","IMPRINT",EDGE,{"derivedFrom":subQ5}),1.0]])]});}
            var Q1;
            Q1=makeQuery(id+"F9.opExtrude","CAP_FACE",FACE,{"disambiguationData":[OSD([sQuery(id+"F1.wireOp",EDGE,"E7"),sQuery(id+"F1.wireOp",EDGE,"E8"),sQuery(id+"F1.wireOp",EDGE,"E9"),sQuery(id+"F1.wireOp",EDGE,"E10"),sQuery(id+"F1.wireOp",EDGE,"E11"),sQuery(id+"F1.wireOp",EDGE,"E12"),sQuery(id+"F1.wireOp",EDGE,"E13"),sQuery(id+"F1.wireOp",EDGE,"E14"),sQuery(id+"F1.wireOp",EDGE,"E17"),sQuery(id+"F1.wireOp",EDGE,"E18"),sQuery(id+"F1.wireOp",EDGE,"E20"),sQuery(id+"F1.wireOp",EDGE,"E21"),sQuery(id+"F1.wireOp",EDGE,"E22"),sQuery(id+"F1.wireOp",EDGE,"E23"),sQuery(id+"F1.wireOp",EDGE,"E24"),sQuery(id+"F1.wireOp",EDGE,"E25"),sQuery(id+"F1.wireOp",EDGE,"E26"),sQuery(id+"F1.wireOp",EDGE,"E27"),sQuery(id+"F1.wireOp",EDGE,"E28"),sQuery(id+"F1.wireOp",EDGE,"E29"),sQuery(id+"F1.wireOp",EDGE,"E30"),sQuery(id+"F1.wireOp",EDGE,"E31"),sQuery(id+"F1.wireOp",EDGE,"E32"),sQuery(id+"F1.wireOp",EDGE,"E33"),sQuery(id+"F1.wireOp",EDGE,"E34"),sQuery(id+"F1.wireOp",EDGE,"E35"),sQuery(id+"F1.wireOp",EDGE,"E36"),sQuery(id+"F1.wireOp",EDGE,"E37"),sQuery(id+"F1.wireOp",EDGE,"E38"),sQuery(id+"F1.wireOp",EDGE,"E39"),sQuery(id+"F1.wireOp",EDGE,"E40"),sQuery(id+"F1.wireOp",EDGE,"E41"),sQuery(id+"F1.wireOp",EDGE,"E42"),sQuery(id+"F1.wireOp",EDGE,"E50"),sQuery(id+"F1.wireOp",EDGE,"E51")])],"isStart":false});
            extrude(context, id + "F10", {"entities" : qUnion([Q0]), "operationType" : NewBodyOperationType.ADD, "endBound" : BoundingType.UP_TO_SURFACE, "oppositeDirection" : true, "depth" : 25 * mm, "endBoundEntityFace" : qUnion([Q1]), "offsetDistance" : 25 * mm, "hasSecondDirection" : true, "secondDirectionOppositeDirection" : true, "secondDirectionDepth" : 10 * mm});
        }
        {
            var Q0;
            {var subQ0=sQuery(id+"F1.wireOp",EDGE,"E39");var subQ1=sQuery(id+"F1.wireOp",EDGE,"E38");var subQ2=sQuery(id+"F1.wireOp",EDGE,"E37");var subQ3=sQuery(id+"F1.wireOp",EDGE,"E26");var subQ4=sQuery(id+"F1.wireOp",EDGE,"E25");var subQ5=sQuery(id+"F1.wireOp",EDGE,"E24");Q0=makeQuery(id+"F10.boolean.opBoolean","MERGE",FACE,{"derivedFrom":[makeQuery(id+"F9.opExtrude","CAP_FACE",FACE,{"disambiguationData":[OSD([sQuery(id+"F1.wireOp",EDGE,"E7"),sQuery(id+"F1.wireOp",EDGE,"E8"),sQuery(id+"F1.wireOp",EDGE,"E9"),sQuery(id+"F1.wireOp",EDGE,"E10"),sQuery(id+"F1.wireOp",EDGE,"E11"),sQuery(id+"F1.wireOp",EDGE,"E12"),sQuery(id+"F1.wireOp",EDGE,"E13"),sQuery(id+"F1.wireOp",EDGE,"E14"),sQuery(id+"F1.wireOp",EDGE,"E17"),sQuery(id+"F1.wireOp",EDGE,"E18"),sQuery(id+"F1.wireOp",EDGE,"E20"),sQuery(id+"F1.wireOp",EDGE,"E21"),sQuery(id+"F1.wireOp",EDGE,"E22"),sQuery(id+"F1.wireOp",EDGE,"E23"),subQ5,subQ4,subQ3,sQuery(id+"F1.wireOp",EDGE,"E27"),sQuery(id+"F1.wireOp",EDGE,"E28"),sQuery(id+"F1.wireOp",EDGE,"E29"),sQuery(id+"F1.wireOp",EDGE,"E30"),sQuery(id+"F1.wireOp",EDGE,"E31"),sQuery(id+"F1.wireOp",EDGE,"E32"),sQuery(id+"F1.wireOp",EDGE,"E33"),sQuery(id+"F1.wireOp",EDGE,"E34"),sQuery(id+"F1.wireOp",EDGE,"E35"),sQuery(id+"F1.wireOp",EDGE,"E36"),subQ2,subQ1,subQ0,sQuery(id+"F1.wireOp",EDGE,"E40"),sQuery(id+"F1.wireOp",EDGE,"E41"),sQuery(id+"F1.wireOp",EDGE,"E42"),sQuery(id+"F1.wireOp",EDGE,"E50"),sQuery(id+"F1.wireOp",EDGE,"E51")])],"isStart":false}),makeQuery(id+"F10.opExtrude","CAP_FACE",FACE,{"disambiguationData":[OSD([subQ5,subQ4,subQ3,subQ2,subQ1,subQ0,sQuery(id+"F1.wireOp",EDGE,"E43"),sQuery(id+"F1.wireOp",EDGE,"E46"),sQuery(id+"F1.wireOp",EDGE,"E47"),sQuery(id+"F1.wireOp",EDGE,"E48"),sQuery(id+"F1.wireOp",EDGE,"E49")])],"isStart":false})]});}
            var sketch = newSketch(context, id + "F11", { "sketchPlane" : qUnion([Q0])});
            skLineSegment(sketch, "E59", {"start": v(-54.5, 14) * mm, "end": v(-53.5, 14) * mm});
            skLineSegment(sketch, "E60", {"start": v(-54.5, 5.5) * mm, "end": v(-53.5, 5.5) * mm});
            skLineSegment(sketch, "E61", {"start": v(-54.5, -29.25) * mm, "end": v(-53.5, -29.25) * mm});
            skLineSegment(sketch, "E62", {"start": v(-53.5, -40) * mm, "end": v(-54.5, -40) * mm});
            skLineSegment(sketch, "E63", {"start": v(-50.5, 20) * mm, "end": v(-50.5, 35.5) * mm});
            skLineSegment(sketch, "E64", {"start": v(-50.5, -26) * mm, "end": v(-50.5, -3) * mm});
            skSolve(sketch);
        }
        {
            var Q0;
            {var subQ0=sQuery(id+"F11.wireOp",EDGE,"E61");Q0=makeQuery(id+"F11.imprint","IMPRINT",FACE,{"disambiguationData":[TD([[makeQuery(id+"F11.imprint","IMPRINT",EDGE,{"derivedFrom":subQ0}),-1.0]])]});}
            extrude(context, id + "F12", {"entities" : qUnion([Q0]), "operationType" : NewBodyOperationType.REMOVE, "endBound" : BoundingType.THROUGH_ALL, "oppositeDirection" : true, "depth" : 25 * mm, "offsetDistance" : 25 * mm, "hasSecondDirection" : true, "secondDirectionOppositeDirection" : true, "secondDirectionDepth" : 4.25 * mm});
        }
        {
            var Q0;
            {var subQ0=sQuery(id+"F11.wireOp",EDGE,"E59");Q0=makeQuery(id+"F11.imprint","IMPRINT",FACE,{"disambiguationData":[TD([[makeQuery(id+"F11.imprint","IMPRINT",EDGE,{"derivedFrom":subQ0}),-1.0]])]});}
            extrude(context, id + "F13", {"entities" : qUnion([Q0]), "operationType" : NewBodyOperationType.REMOVE, "endBound" : BoundingType.THROUGH_ALL, "oppositeDirection" : true, "depth" : 25 * mm, "offsetDistance" : 25 * mm, "hasSecondDirection" : true, "secondDirectionOppositeDirection" : true, "secondDirectionDepth" : 7.6 * mm});
        }
        {
            var Q0;
            {var subQ0=sQuery(id+"F11.wireOp",EDGE,"E63");Q0=makeQuery(id+"F11.imprint","IMPRINT",FACE,{"disambiguationData":[TD([[makeQuery(id+"F11.imprint","IMPRINT",EDGE,{"derivedFrom":subQ0}),1.0]])]});}
            var Q1;
            Q1=makeQuery(id+"F11.imprint","IMPRINT",FACE,{"disambiguationData":[TD([[makeQuery(id+"F11.imprint","IMPRINT",EDGE,{"derivedFrom":sQuery(id+"F11.wireOp",EDGE,"E64")}),1.0]])]});
            var Q2;
            {var subQ0=sQuery(id+"F1.wireOp",EDGE,"E35");var subQ1=sQuery(id+"F1.wireOp",EDGE,"E34");var subQ2=sQuery(id+"F1.wireOp",EDGE,"E33");var subQ3=sQuery(id+"F1.wireOp",EDGE,"E32");var subQ4=sQuery(id+"F1.wireOp",EDGE,"E31");var subQ5=sQuery(id+"F1.wireOp",EDGE,"E30");var subQ6=sQuery(id+"F1.wireOp",EDGE,"E13");var subQ7=sQuery(id+"F1.wireOp",EDGE,"E27");var subQ8=sQuery(id+"F1.wireOp",EDGE,"E28");var subQ9=sQuery(id+"F1.wireOp",EDGE,"E29");Q2=makeQuery(id+"F13.boolean.opBoolean","SPLIT",FACE,{"disambiguationData":[TD([makeQuery(id+"F9.opExtrude","SWEPT_FACE",FACE,{"disambiguationData":[OSD([subQ8])]})])],"derivedFrom":makeQuery(id+"F9.opExtrude","CAP_FACE",FACE,{"disambiguationData":[OSD([sQuery(id+"F1.wireOp",EDGE,"E7"),sQuery(id+"F1.wireOp",EDGE,"E8"),sQuery(id+"F1.wireOp",EDGE,"E9"),sQuery(id+"F1.wireOp",EDGE,"E10"),sQuery(id+"F1.wireOp",EDGE,"E11"),sQuery(id+"F1.wireOp",EDGE,"E12"),subQ6,sQuery(id+"F1.wireOp",EDGE,"E14"),sQuery(id+"F1.wireOp",EDGE,"E17"),sQuery(id+"F1.wireOp",EDGE,"E18"),sQuery(id+"F1.wireOp",EDGE,"E20"),sQuery(id+"F1.wireOp",EDGE,"E21"),sQuery(id+"F1.wireOp",EDGE,"E22"),sQuery(id+"F1.wireOp",EDGE,"E23"),sQuery(id+"F1.wireOp",EDGE,"E24"),sQuery(id+"F1.wireOp",EDGE,"E25"),sQuery(id+"F1.wireOp",EDGE,"E26"),subQ7,subQ8,subQ9,subQ5,subQ4,subQ3,subQ2,subQ1,subQ0,sQuery(id+"F1.wireOp",EDGE,"E36"),sQuery(id+"F1.wireOp",EDGE,"E37"),sQuery(id+"F1.wireOp",EDGE,"E38"),sQuery(id+"F1.wireOp",EDGE,"E39"),sQuery(id+"F1.wireOp",EDGE,"E40"),sQuery(id+"F1.wireOp",EDGE,"E41"),sQuery(id+"F1.wireOp",EDGE,"E42"),sQuery(id+"F1.wireOp",EDGE,"E50"),sQuery(id+"F1.wireOp",EDGE,"E51")])],"isStart":true})});}
            extrude(context, id + "F14", {"entities" : qUnion([Q0, Q1]), "operationType" : NewBodyOperationType.ADD, "endBound" : BoundingType.UP_TO_SURFACE, "oppositeDirection" : true, "depth" : 25 * mm, "endBoundEntityFace" : qUnion([Q2]), "offsetDistance" : 25 * mm});
        }
        {
            var Q0;
            Q0=makeQuery(id+"F11.imprint","IMPRINT",FACE,{"disambiguationData":[TD([[makeQuery(id+"F11.imprint","IMPRINT",EDGE,{"derivedFrom":makeQuery(id+"F9.opExtrude","CAP_EDGE",EDGE,{"disambiguationData":[OSD([sQuery(id+"F1.wireOp",EDGE,"E21")])],"isStart":false})}),1.0]])]});
            var Q1;
            Q1=makeQuery(id+"F11.imprint","IMPRINT",FACE,{"disambiguationData":[TD([[makeQuery(id+"F11.imprint","IMPRINT",EDGE,{"derivedFrom":makeQuery(id+"F9.opExtrude","CAP_EDGE",EDGE,{"disambiguationData":[OSD([sQuery(id+"F1.wireOp",EDGE,"E17")])],"isStart":false})}),-1.0]])]});
            var Q2;
            Q2=makeQuery(id+"F11.imprint","IMPRINT",FACE,{"disambiguationData":[TD([[makeQuery(id+"F11.imprint","IMPRINT",EDGE,{"derivedFrom":makeQuery(id+"F10.opExtrude","CAP_EDGE",EDGE,{"disambiguationData":[OSD([sQuery(id+"F1.wireOp",EDGE,"E49")])],"isStart":false})}),1.0]])]});
            var Q3;
            Q3=makeQuery(id+"F11.imprint","IMPRINT",FACE,{"disambiguationData":[TD([[makeQuery(id+"F11.imprint","IMPRINT",EDGE,{"derivedFrom":makeQuery(id+"F10.opExtrude","CAP_EDGE",EDGE,{"disambiguationData":[OSD([sQuery(id+"F1.wireOp",EDGE,"E47")])],"isStart":false})}),1.0]])]});
            var Q4;
            Q4=makeQuery(id+"F11.imprint","IMPRINT",FACE,{"disambiguationData":[TD([[makeQuery(id+"F11.imprint","IMPRINT",EDGE,{"derivedFrom":makeQuery(id+"F10.opExtrude","CAP_EDGE",EDGE,{"disambiguationData":[OSD([sQuery(id+"F1.wireOp",EDGE,"E46")])],"isStart":false})}),1.0]])]});
            var Q5;
            Q5=makeQuery(id+"F11.imprint","IMPRINT",FACE,{"disambiguationData":[TD([[makeQuery(id+"F11.imprint","IMPRINT",EDGE,{"derivedFrom":makeQuery(id+"F9.opExtrude","CAP_EDGE",EDGE,{"disambiguationData":[OSD([sQuery(id+"F1.wireOp",EDGE,"E14")])],"isStart":false})}),-1.0]])]});
            var Q6;
            Q6=makeQuery(id+"F11.imprint","IMPRINT",FACE,{"disambiguationData":[TD([[makeQuery(id+"F11.imprint","IMPRINT",EDGE,{"derivedFrom":makeQuery(id+"F10.opExtrude","CAP_EDGE",EDGE,{"disambiguationData":[OSD([sQuery(id+"F1.wireOp",EDGE,"E48")])],"isStart":false})}),1.0]])]});
            var Q7;
            Q7=makeQuery(id+"F11.imprint","IMPRINT",FACE,{"disambiguationData":[TD([[makeQuery(id+"F11.imprint","IMPRINT",EDGE,{"derivedFrom":makeQuery(id+"F9.opExtrude","CAP_EDGE",EDGE,{"disambiguationData":[OSD([sQuery(id+"F1.wireOp",EDGE,"E18")])],"isStart":false})}),-1.0]])]});
            var Q8;
            Q8=makeQuery(id+"F10.opExtrude","CAP_FACE",FACE,{"disambiguationData":[OSD([sQuery(id+"F1.wireOp",EDGE,"E24"),sQuery(id+"F1.wireOp",EDGE,"E25"),sQuery(id+"F1.wireOp",EDGE,"E26"),sQuery(id+"F1.wireOp",EDGE,"E37"),sQuery(id+"F1.wireOp",EDGE,"E38"),sQuery(id+"F1.wireOp",EDGE,"E39"),sQuery(id+"F1.wireOp",EDGE,"E43"),sQuery(id+"F1.wireOp",EDGE,"E46"),sQuery(id+"F1.wireOp",EDGE,"E47"),sQuery(id+"F1.wireOp",EDGE,"E48"),sQuery(id+"F1.wireOp",EDGE,"E49")])],"isStart":true});
            extrude(context, id + "F15", {"entities" : qUnion([Q0, Q1, Q2, Q3, Q4, Q5, Q6, Q7]), "operationType" : NewBodyOperationType.ADD, "endBound" : BoundingType.UP_TO_SURFACE, "oppositeDirection" : true, "depth" : 25 * mm, "endBoundEntityFace" : qUnion([Q8]), "offsetDistance" : 25 * mm});
        }
        {
            var Q0;
            Q0=makeQuery(id+"F2.opExtrude","CAP_EDGE",EDGE,{"disambiguationData":[OSD([sQuery(id+"F1.wireOp",EDGE,"E13")])],"isStart":false});
            var Q1;
            Q1=makeQuery(id+"F2.opExtrude","CAP_EDGE",EDGE,{"disambiguationData":[OSD([sQuery(id+"F1.wireOp",EDGE,"gnJz5Qc8-ZNcq-LTVa-uIN5-WBNiVvJ7uBc6")])],"isStart":false});
            var Q2;
            Q2=makeQuery(id+"F2.opExtrude","CAP_EDGE",EDGE,{"disambiguationData":[OSD([sQuery(id+"F1.wireOp",EDGE,"E12")])],"isStart":false});
            var Q3;
            Q3=makeQuery(id+"F2.opExtrude","CAP_EDGE",EDGE,{"disambiguationData":[OSD([sQuery(id+"F1.wireOp",EDGE,"E7")])],"isStart":false});
            var Q4;
            Q4=makeQuery(id+"F2.opExtrude","CAP_EDGE",EDGE,{"disambiguationData":[OSD([sQuery(id+"F1.wireOp",EDGE,"E8")])],"isStart":false});
            var Q5;
            Q5=makeQuery(id+"F2.opExtrude","CAP_EDGE",EDGE,{"disambiguationData":[OSD([sQuery(id+"F1.wireOp",EDGE,"E10")])],"isStart":false});
            var Q6;
            Q6=makeQuery(id+"F2.opExtrude","CAP_EDGE",EDGE,{"disambiguationData":[OSD([sQuery(id+"F1.wireOp",EDGE,"E11")])],"isStart":false});
            var Q7;
            Q7=makeQuery(id+"F2.opExtrude","CAP_EDGE",EDGE,{"disambiguationData":[OSD([sQuery(id+"F1.wireOp",EDGE,"E9")])],"isStart":false});
            var Q8;
            Q8=makeQuery(id+"F9.opExtrude","CAP_EDGE",EDGE,{"disambiguationData":[OSD([sQuery(id+"F1.wireOp",EDGE,"E13")])],"isStart":false});
            var Q9;
            Q9=makeQuery(id+"F9.opExtrude","CAP_EDGE",EDGE,{"disambiguationData":[OSD([sQuery(id+"F1.wireOp",EDGE,"E50")])],"isStart":false});
            var Q10;
            Q10=makeQuery(id+"F9.opExtrude","CAP_EDGE",EDGE,{"disambiguationData":[OSD([sQuery(id+"F1.wireOp",EDGE,"E12")])],"isStart":false});
            var Q11;
            Q11=makeQuery(id+"F9.opExtrude","CAP_EDGE",EDGE,{"disambiguationData":[OSD([sQuery(id+"F1.wireOp",EDGE,"E11")])],"isStart":false});
            var Q12;
            Q12=makeQuery(id+"F9.opExtrude","CAP_EDGE",EDGE,{"disambiguationData":[OSD([sQuery(id+"F1.wireOp",EDGE,"E10")])],"isStart":false});
            var Q13;
            Q13=makeQuery(id+"F9.opExtrude","CAP_EDGE",EDGE,{"disambiguationData":[OSD([sQuery(id+"F1.wireOp",EDGE,"E7")])],"isStart":false});
            var Q14;
            Q14=makeQuery(id+"F9.opExtrude","CAP_EDGE",EDGE,{"disambiguationData":[OSD([sQuery(id+"F1.wireOp",EDGE,"E8")])],"isStart":false});
            var Q15;
            Q15=makeQuery(id+"F9.opExtrude","CAP_EDGE",EDGE,{"disambiguationData":[OSD([sQuery(id+"F1.wireOp",EDGE,"E9")])],"isStart":false});
            chamfer(context, id + "F16", {"entities" : qUnion([Q0, Q1, Q2, Q3, Q4, Q5, Q6, Q7, Q8, Q9, Q10, Q11, Q12, Q13, Q14, Q15]), "width" : 1.5 * mm, "tangentPropagation" : true});
        }
        {
            var Q0;
            Q0=makeQuery(id+"F1.imprint","IMPRINT",FACE,{"disambiguationData":[TD([[makeQuery(id+"F1.imprint","IMPRINT",EDGE,{"derivedFrom":sQuery(id+"F1.wireOp",EDGE,"E15")}),-1.0]])]});
            var Q1;
            Q1=makeQuery(id+"F1.imprint","IMPRINT",FACE,{"disambiguationData":[TD([[makeQuery(id+"F1.imprint","IMPRINT",EDGE,{"derivedFrom":sQuery(id+"F1.wireOp",EDGE,"E16")}),-1.0]])]});
            var Q2;
            {var subQ0=sQuery(id+"F1.wireOp",EDGE,"E49");var subQ1=sQuery(id+"F1.wireOp",EDGE,"E48");var subQ2=sQuery(id+"F1.wireOp",EDGE,"E47");var subQ3=sQuery(id+"F1.wireOp",EDGE,"E46");var subQ4=sQuery(id+"F1.wireOp",EDGE,"E51");var subQ5=sQuery(id+"F1.wireOp",EDGE,"E43");var subQ6=sQuery(id+"F1.wireOp",EDGE,"E42");var subQ7=sQuery(id+"F1.wireOp",EDGE,"E41");var subQ8=sQuery(id+"F1.wireOp",EDGE,"E40");var subQ9=sQuery(id+"F1.wireOp",EDGE,"E37");var subQ10=sQuery(id+"F1.wireOp",EDGE,"E36");var subQ11=sQuery(id+"F1.wireOp",EDGE,"E35");var subQ12=sQuery(id+"F1.wireOp",EDGE,"E34");var subQ13=sQuery(id+"F1.wireOp",EDGE,"E33");var subQ14=sQuery(id+"F1.wireOp",EDGE,"E32");var subQ15=sQuery(id+"F1.wireOp",EDGE,"E31");var subQ16=sQuery(id+"F1.wireOp",EDGE,"E30");var subQ17=sQuery(id+"F1.wireOp",EDGE,"E29");var subQ18=sQuery(id+"F1.wireOp",EDGE,"E28");var subQ19=sQuery(id+"F1.wireOp",EDGE,"E27");var subQ20=sQuery(id+"F1.wireOp",EDGE,"E24");var subQ21=sQuery(id+"F1.wireOp",EDGE,"E23");var subQ22=sQuery(id+"F1.wireOp",EDGE,"E22");var subQ23=sQuery(id+"F1.wireOp",EDGE,"E21");var subQ24=sQuery(id+"F1.wireOp",EDGE,"E20");var subQ25=sQuery(id+"F1.wireOp",EDGE,"E18");var subQ26=sQuery(id+"F1.wireOp",EDGE,"E17");var subQ27=sQuery(id+"F1.wireOp",EDGE,"E14");var subQ28=sQuery(id+"F1.wireOp",EDGE,"E39");var subQ29=sQuery(id+"F1.wireOp",EDGE,"E38");var subQ30=sQuery(id+"F1.wireOp",EDGE,"E26");var subQ31=sQuery(id+"F1.wireOp",EDGE,"E25");Q2=makeQuery(id+"F15.boolean.opBoolean","MERGE",FACE,{"derivedFrom":[makeQuery(id+"F10.boolean.opBoolean","MERGE",FACE,{"derivedFrom":[makeQuery(id+"F9.opExtrude","CAP_FACE",FACE,{"disambiguationData":[OSD([sQuery(id+"F1.wireOp",EDGE,"E7"),sQuery(id+"F1.wireOp",EDGE,"E8"),sQuery(id+"F1.wireOp",EDGE,"E9"),sQuery(id+"F1.wireOp",EDGE,"E10"),sQuery(id+"F1.wireOp",EDGE,"E11"),sQuery(id+"F1.wireOp",EDGE,"E12"),sQuery(id+"F1.wireOp",EDGE,"E13"),subQ27,subQ26,subQ25,subQ24,subQ23,subQ22,subQ21,subQ20,subQ31,subQ30,subQ19,subQ18,subQ17,subQ16,subQ15,subQ14,subQ13,subQ12,subQ11,subQ10,subQ9,subQ29,subQ28,subQ8,subQ7,subQ6,sQuery(id+"F1.wireOp",EDGE,"E50"),subQ4])],"isStart":false}),makeQuery(id+"F10.opExtrude","CAP_FACE",FACE,{"disambiguationData":[OSD([subQ20,subQ31,subQ30,subQ9,subQ29,subQ28,subQ5,subQ3,subQ2,subQ1,subQ0])],"isStart":false})]}),makeQuery(id+"F15.opExtrude","CAP_FACE",FACE,{"disambiguationData":[OSD([subQ27])],"isStart":true}),makeQuery(id+"F15.opExtrude","CAP_FACE",FACE,{"disambiguationData":[OSD([subQ26])],"isStart":true}),makeQuery(id+"F15.opExtrude","CAP_FACE",FACE,{"disambiguationData":[OSD([subQ25])],"isStart":true}),makeQuery(id+"F15.opExtrude","CAP_FACE",FACE,{"disambiguationData":[OSD([subQ24,subQ23,subQ22,subQ21,subQ20,subQ19,subQ18,subQ17,subQ16,subQ15,subQ14,subQ13,subQ12,subQ11,subQ10,subQ9,subQ8,subQ7,subQ6,subQ5,subQ4])],"isStart":true}),makeQuery(id+"F15.opExtrude","CAP_FACE",FACE,{"disambiguationData":[OSD([subQ3])],"isStart":true}),makeQuery(id+"F15.opExtrude","CAP_FACE",FACE,{"disambiguationData":[OSD([subQ2])],"isStart":true}),makeQuery(id+"F15.opExtrude","CAP_FACE",FACE,{"disambiguationData":[OSD([subQ1])],"isStart":true}),makeQuery(id+"F15.opExtrude","CAP_FACE",FACE,{"disambiguationData":[OSD([subQ0])],"isStart":true})]});}
            extrude(context, id + "F17", {"entities" : qUnion([Q0, Q1]), "operationType" : NewBodyOperationType.ADD, "endBound" : BoundingType.UP_TO_SURFACE, "oppositeDirection" : true, "depth" : 25 * mm, "endBoundEntityFace" : qUnion([Q2]), "offsetDistance" : 25 * mm});
        }
    });
